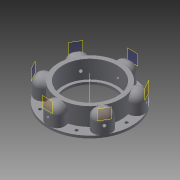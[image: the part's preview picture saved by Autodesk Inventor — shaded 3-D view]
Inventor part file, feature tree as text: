
AUTODESK INVENTOR PART (.ipt)
format: ipt  version: 2015 (Build 190159000, 159)  size: 343,552 bytes
history: native  units: in
note: dims shown in document units (in); Inventor stores cm internally (conversion verified against a paired STEP export)
features: plane x7, sketch x7, pattern_circular x5, extrude x4, hole x4, fillet x1
ambient origin geometry x8: Origin, YZ Plane, XZ Plane, XY Plane, X Axis, Y Axis, Z Axis, Center Point
bodies: Solid1 (feature_tree)
feature tree (28):
  extrude  "Extrusion1"  Depth=7.0in
  extrude  "Extrusion4"  Depth=5.21in
  hole  "Hole4"  [1 undecoded]
  pattern_circular  "Circular Pattern4"  Count=6 Angle=360.0deg
  extrude  "Extrusion5"  Depth=0.625in
  plane  "Work Plane4"
  hole  "Hole5"  [1 undecoded]
  fillet  "Fillet1"  Radius=0.895in
  pattern_circular  "Circular Pattern6"  [2 undecoded]
  pattern_circular  "Circular Pattern5"  [2 undecoded]
  hole  "Hole1"  [1 undecoded]
  pattern_circular  "Circular Pattern1"  Count=6 Angle=360.0deg
  extrude  "Extrusion3"  TaperAngle=30.0deg  [1 undecoded]
  plane  "Work Plane3"
  hole  "Hole3"  [1 undecoded]
  pattern_circular  "Circular Pattern3"  [2 undecoded]
  sketch  "Sketch1"  dims[d0=4.026in d1=7.0in]
  sketch  "Sketch2"  dims[d2=0.2in d3=0.0in d4=5.21in]
  sketch  "Sketch4"  dims[d12=0.25in d13=0.75in d14=0.375in d15=0.25in d16=0.5635in d17=1.0in d18=0.8108in d19=2.3622in d20=360.0deg]
  sketch  "Sketch6"  dims[d22=1.51in d23=0.0in]
  sketch  "Sketch9"  dims[d35=0.855in]
  sketch  "Sketch11"  dims[d36=0.25in]
  sketch  "Sketch12"  dims[d37=0.25in d38=0.75in d39=0.375in d40=0.25in d41=0.5635in d42=1.5425in d43=0.8108in d44=2.3622in d45=360.0deg d47=4.5in d48=1.5in d49=0.0in d50=0.895in d51=0.25in d52=0.895in d54=0.25in d55=0.25in d56=0.75in d57=0.375in d58=0.25in d59=0.5635in d60=1.0in d61=0.8108in d62=2.3622in d63=360.0deg d71=30.0deg d72=1.5in d73=0.0in d74=0.85in d75=0.25in d76=0.25in d77=0.75in d78=0.375in d79=0.25in d80=0.5635in d81=2.0in d82=0.0in d83=2.3622in d84=360.0deg d86=0.625in d87=2.3622in d88=360.0deg]
  plane  "Work Plane5"
  plane  "Work Plane6"
  plane  "Work Plane7"
  plane  "Work Plane8"
  plane  "Work Plane9"
note: 11 required parameter values undecoded (feature->parameter linkage not recoverable at this tier; creation-order binding heuristic only, values carry confidence <= 0.55)
